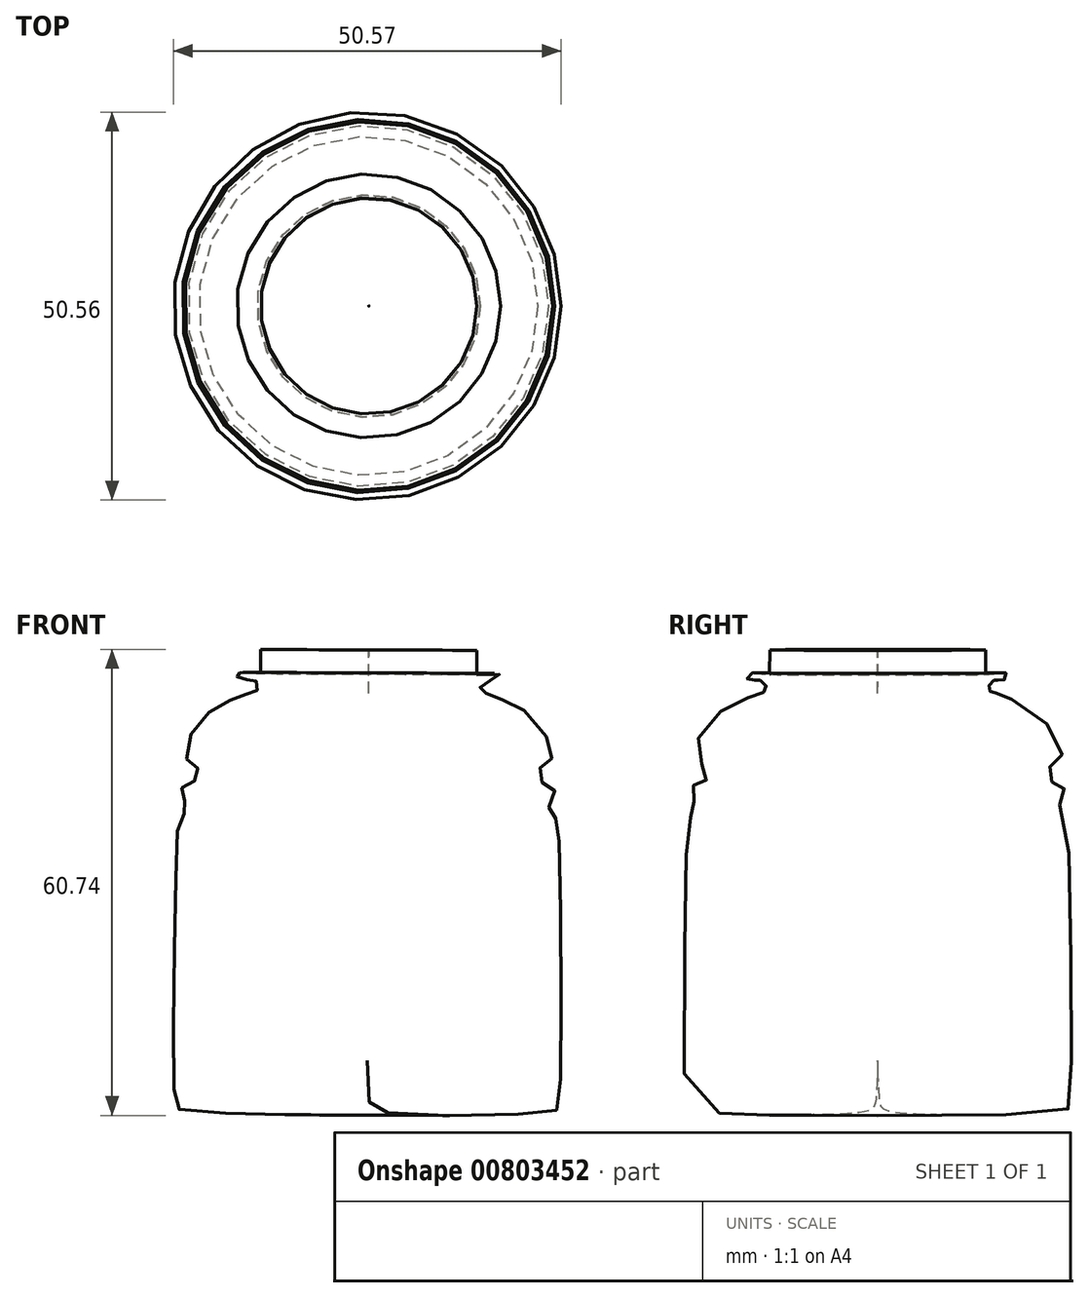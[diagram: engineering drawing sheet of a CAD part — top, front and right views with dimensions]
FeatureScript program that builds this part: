
annotation { "Feature Type Name" : "Feature", "Feature Type Description" : "" }
export const myFeature = defineFeature(function(context is Context, id is Id, definition is map)
    precondition{}
    {
        {
            var Q0;
            Q0=qCreatedBy(makeId("Front.planeOp"),FACE);
            var sketch = newSketch(context, id + "F0", { "sketchPlane" : qUnion([Q0])});
            skLineSegment(sketch, "E0.bottom", {"start": v(-41.5, 58.56) * mm, "end": v(41.82, 58.56) * mm});
            skLineSegment(sketch, "E0.top", {"start": v(-41.5, -69.26) * mm, "end": v(41.82, -69.26) * mm});
            skLineSegment(sketch, "E0.left", {"start": v(-41.5, 58.56) * mm, "end": v(-41.5, -69.26) * mm});
            skLineSegment(sketch, "E0.right", {"start": v(41.82, 58.56) * mm, "end": v(41.82, -69.26) * mm});
            skFitSpline(sketch, "E1", {"points": [v(14.05, 58.56) * mm, v(14.05, 55.37) * mm], "startDerivative": vector(0, -9.59) * mm, "endDerivative": vector(0, -9.59) * mm});
            skFitSpline(sketch, "E2", {"points": [v(14.05, 55.37) * mm, v(17.06, 55.37) * mm, v(16.92, 54.79) * mm, v(14.66, 54.47) * mm, v(14.5, 53.74) * mm, v(14.5, 53.22) * mm, v(15.3, 52.94) * mm, v(17, 52.25) * mm, v(20.12, 50.8) * mm, v(23.92, 45.51) * mm, v(23.42, 44.03) * mm, v(22.26, 43.2) * mm, v(22.26, 41.55) * mm, v(23.92, 40.89) * mm, v(24.08, 39.23) * mm, v(23.42, 37.75) * mm, v(24.25, 36.75) * mm, v(24.74, 34.6) * mm, v(24.9, 0) * mm, v(23.59, -1.6) * mm, v(1.44, -1.6) * mm, v(0, 0) * mm, v(0, 58.56) * mm], "startDerivative": vector(121.88, 11.24) * mm, "endDerivative": vector(4.96, 488.54) * mm});
            skLineSegment(sketch, "E3", {"start": v(0, 58.56) * mm, "end": v(14.05, 58.56) * mm});
            skLineSegment(sketch, "E4", {"start": v(0, 68.13) * mm, "end": v(-0.29, -8.94) * mm});
            skSolve(sketch);
        }
        {
            var Q0;
            {var subQ4=sQuery(id+"F0.wireOp",EDGE,"E1");Q0=makeQuery(id+"F0.imprint","IMPRINT",FACE,{"disambiguationData":[TD([[makeQuery(id+"F0.imprint","IMPRINT",EDGE,{"derivedFrom":subQ4}),-1.0]])]});}
            var Q1;
            Q1=sQuery(id+"F0.wireOp",EDGE,"E4");
            revolve(context, id + "F1", {"surfaceOperationType" : NewSurfaceOperationType.NEW, "entities" : qUnion([Q0]), "axis" : qUnion([Q1]), "revolveType" : RevolveType.FULL});
        }
    });
